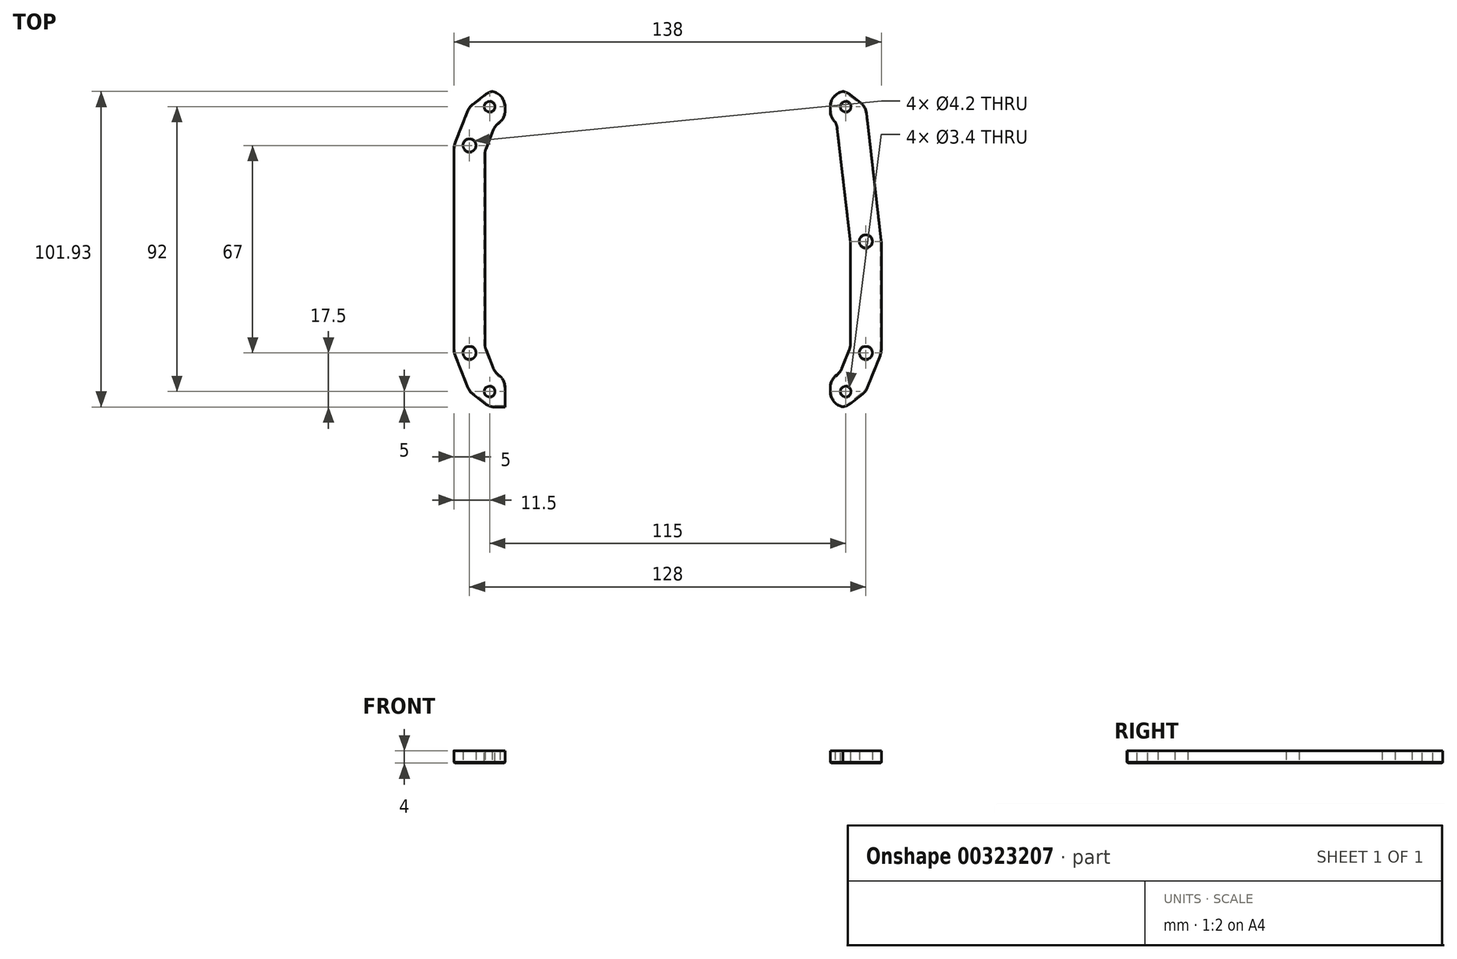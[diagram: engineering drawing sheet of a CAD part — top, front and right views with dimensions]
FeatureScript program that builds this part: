
annotation { "Feature Type Name" : "Feature", "Feature Type Description" : "" }
export const myFeature = defineFeature(function(context is Context, id is Id, definition is map)
    precondition{}
    {
        {
            var Q0;
            Q0=qCreatedBy(makeId("Top.planeOp"),FACE);
            var sketch = newSketch(context, id + "F0", { "sketchPlane" : qUnion([Q0])});
            skLineSegment(sketch, "E0", {"start": v(-64, 33.5) * mm, "end": v(-64, -33.5) * mm, "construction": true});
            skLineSegment(sketch, "E1", {"start": v(-64, -33.5) * mm, "end": v(64, -33.5) * mm, "construction": true});
            skLineSegment(sketch, "E2", {"start": v(64, -33.5) * mm, "end": v(64, 2.5) * mm, "construction": true});
            skLineSegment(sketch, "E3", {"start": v(0, 0) * mm, "end": v(0, -33.5) * mm, "construction": true});
            skCircle(sketch, "E4", {"center": v(-64, 33.5) * mm, "radius": 2.1 * mm});
            skCircle(sketch, "E5", {"center": v(-64, -33.5) * mm, "radius": 2.1 * mm});
            skCircle(sketch, "E6", {"center": v(64, -33.5) * mm, "radius": 2.1 * mm});
            skCircle(sketch, "E7", {"center": v(64, 2.5) * mm, "radius": 2.1 * mm});
            skSolve(sketch);
        }
        {
            var Q0;
            Q0=qCreatedBy(makeId("Top.planeOp"),FACE);
            var sketch = newSketch(context, id + "F1", { "sketchPlane" : qUnion([Q0])});
            skLineSegment(sketch, "E8.bottom", {"start": v(57.5, 46) * mm, "end": v(-57.5, 46) * mm, "construction": true});
            skLineSegment(sketch, "E8.top", {"start": v(57.5, -46) * mm, "end": v(-57.5, -46) * mm, "construction": true});
            skLineSegment(sketch, "E8.left", {"start": v(57.5, 46) * mm, "end": v(57.5, -46) * mm, "construction": true});
            skLineSegment(sketch, "E8.right", {"start": v(-57.5, 46) * mm, "end": v(-57.5, -46) * mm, "construction": true});
            skPoint(sketch, "E8.middle", {"position": v(0, 0) * mm});
            skCircle(sketch, "E9", {"center": v(-57.5, 46) * mm, "radius": 2.1 * mm});
            skCircle(sketch, "E10", {"center": v(57.5, 46) * mm, "radius": 2.1 * mm});
            skCircle(sketch, "E11", {"center": v(57.5, -46) * mm, "radius": 2.1 * mm});
            skCircle(sketch, "E12", {"center": v(-57.5, -46) * mm, "radius": 2.1 * mm});
            skSolve(sketch);
        }
        {
            var Q0;
            Q0=qCreatedBy(makeId("Top.planeOp"),FACE);
            var sketch = newSketch(context, id + "F2", { "sketchPlane" : qUnion([Q0])});
            skLineSegment(sketch, "E13", {"start": v(-69, 33.5) * mm, "end": v(-69, -33.5) * mm});
            skLineSegment(sketch, "E14", {"start": v(-57.5, -51) * mm, "end": v(57.5, -51) * mm});
            skLineSegment(sketch, "E15", {"start": v(69, -33.5) * mm, "end": v(69, 2.5) * mm});
            skLineSegment(sketch, "E16", {"start": v(57.5, 51) * mm, "end": v(-57.5, 51) * mm});
            skLineSegment(sketch, "E17", {"start": v(-69, 33.5) * mm, "end": v(-64, 46) * mm});
            skLineSegment(sketch, "E18", {"start": v(-64, 46) * mm, "end": v(-57.5, 51) * mm});
            skLineSegment(sketch, "E19", {"start": v(57.5, 51) * mm, "end": v(64, 46) * mm});
            skLineSegment(sketch, "E20", {"start": v(64, 46) * mm, "end": v(69, 2.5) * mm});
            skLineSegment(sketch, "E21", {"start": v(57.5, -51) * mm, "end": v(64, -46) * mm});
            skLineSegment(sketch, "E22", {"start": v(64, -46) * mm, "end": v(69, -33.5) * mm});
            skLineSegment(sketch, "E23", {"start": v(-57.5, -51) * mm, "end": v(-64, -46) * mm});
            skLineSegment(sketch, "E24", {"start": v(-64, -46) * mm, "end": v(-69, -33.5) * mm});
            skLineSegment(sketch, "E25.0", {"start": v(55.73, -39.74) * mm, "end": v(59, -31.57) * mm});
            skLineSegment(sketch, "E25.1", {"start": v(-55.73, 39.74) * mm, "end": v(-54.1, 41) * mm});
            skLineSegment(sketch, "E25.2", {"start": v(54.1, 41) * mm, "end": v(-54.1, 41) * mm});
            skLineSegment(sketch, "E25.3", {"start": v(54.1, 41) * mm, "end": v(54.55, 40.65) * mm});
            skLineSegment(sketch, "E25.4", {"start": v(54.55, 40.65) * mm, "end": v(59, 1.93) * mm});
            skLineSegment(sketch, "E25.5", {"start": v(-59, 31.57) * mm, "end": v(-55.73, 39.74) * mm});
            skLineSegment(sketch, "E25.6", {"start": v(59, -31.57) * mm, "end": v(59, 1.93) * mm});
            skLineSegment(sketch, "E25.7", {"start": v(-59, 31.57) * mm, "end": v(-59, -31.57) * mm});
            skLineSegment(sketch, "E25.8", {"start": v(-55.73, -39.74) * mm, "end": v(-59, -31.57) * mm});
            skLineSegment(sketch, "E25.9", {"start": v(-54.1, -41) * mm, "end": v(-55.73, -39.74) * mm});
            skLineSegment(sketch, "E25.10", {"start": v(-54.1, -41) * mm, "end": v(54.1, -41) * mm});
            skLineSegment(sketch, "E25.11", {"start": v(54.1, -41) * mm, "end": v(55.73, -39.74) * mm});
            skSolve(sketch);
        }
        {
            var Q0;
            Q0=makeQuery(id+"F2.imprint","IMPRINT",FACE,{"disambiguationData":[TD([[makeQuery(id+"F2.imprint","IMPRINT",EDGE,{"derivedFrom":sQuery(id+"F2.wireOp",EDGE,"E13")}),1.0]])]});
            extrude(context, id + "F3", {"entities" : qUnion([Q0]), "depth" : 4 * mm});
        }
        {
            var Q0;
            Q0=qSketchRegion(id+"F0",true);
            extrude(context, id + "F4", {"entities" : qUnion([Q0]), "operationType" : NewBodyOperationType.REMOVE, "endBound" : BoundingType.THROUGH_ALL, "depth" : 25 * mm});
        }
        {
            var Q0;
            Q0=makeQuery(id+"F3.opExtrude","CAP_FACE",FACE,{"disambiguationData":[OSD([sQuery(id+"F2.wireOp",EDGE,"E13"),sQuery(id+"F2.wireOp",EDGE,"E14"),sQuery(id+"F2.wireOp",EDGE,"E15"),sQuery(id+"F2.wireOp",EDGE,"E16"),sQuery(id+"F2.wireOp",EDGE,"E17"),sQuery(id+"F2.wireOp",EDGE,"E18"),sQuery(id+"F2.wireOp",EDGE,"E19"),sQuery(id+"F2.wireOp",EDGE,"E20"),sQuery(id+"F2.wireOp",EDGE,"E21"),sQuery(id+"F2.wireOp",EDGE,"E22"),sQuery(id+"F2.wireOp",EDGE,"E23"),sQuery(id+"F2.wireOp",EDGE,"E24"),sQuery(id+"F2.wireOp",EDGE,"E25.0"),sQuery(id+"F2.wireOp",EDGE,"E25.1"),sQuery(id+"F2.wireOp",EDGE,"E25.2"),sQuery(id+"F2.wireOp",EDGE,"E25.3"),sQuery(id+"F2.wireOp",EDGE,"E25.4"),sQuery(id+"F2.wireOp",EDGE,"E25.5"),sQuery(id+"F2.wireOp",EDGE,"E25.6"),sQuery(id+"F2.wireOp",EDGE,"E25.7"),sQuery(id+"F2.wireOp",EDGE,"E25.8"),sQuery(id+"F2.wireOp",EDGE,"E25.9"),sQuery(id+"F2.wireOp",EDGE,"E25.10"),sQuery(id+"F2.wireOp",EDGE,"E25.11")])],"isStart":false});
            var sketch = newSketch(context, id + "F5", { "sketchPlane" : qUnion([Q0])});
            skCircle(sketch, "E26", {"center": v(-57.5, 46) * mm, "radius": 1.7 * mm});
            skCircle(sketch, "E27", {"center": v(57.5, 46) * mm, "radius": 1.7 * mm});
            skCircle(sketch, "E28", {"center": v(57.5, -46) * mm, "radius": 1.7 * mm});
            skCircle(sketch, "E29", {"center": v(-57.5, -46) * mm, "radius": 1.7 * mm});
            skSolve(sketch);
        }
        {
            var Q0;
            Q0=qSketchRegion(id+"F5",true);
            extrude(context, id + "F6", {"entities" : qUnion([Q0]), "operationType" : NewBodyOperationType.REMOVE, "endBound" : BoundingType.THROUGH_ALL, "oppositeDirection" : true, "depth" : 25 * mm});
        }
        {
            var Q0;
            Q0=makeQuery(id+"F3.opExtrude","SWEPT_FACE",FACE,{"disambiguationData":[OSD([sQuery(id+"F2.wireOp",EDGE,"E14")])]});
            var sketch = newSketch(context, id + "F7", { "sketchPlane" : qUnion([Q0])});
            skLineSegment(sketch, "E30.bottom", {"start": v(-52.5, 0) * mm, "end": v(52.5, 0) * mm});
            skLineSegment(sketch, "E30.top", {"start": v(-52.5, 4) * mm, "end": v(52.5, 4) * mm});
            skLineSegment(sketch, "E30.left", {"start": v(-52.5, 0) * mm, "end": v(-52.5, 4) * mm});
            skLineSegment(sketch, "E30.right", {"start": v(52.5, 0) * mm, "end": v(52.5, 4) * mm});
            skSolve(sketch);
        }
        {
            var Q0;
            Q0=qSketchRegion(id+"F7",true);
            extrude(context, id + "F8", {"entities" : qUnion([Q0]), "operationType" : NewBodyOperationType.REMOVE, "endBound" : BoundingType.THROUGH_ALL, "oppositeDirection" : true, "depth" : 25 * mm});
        }
        {
            var Q0;
            Q0=makeQuery(id+"F8.boolean.opBoolean","COPY",EDGE,{"derivedFrom":makeQuery(id+"F8.opExtrude","CAP_EDGE",EDGE,{"disambiguationData":[OSD([sQuery(id+"F7.wireOp",EDGE,"E30.left")])],"isStart":true})});
            var Q1;
            Q1=makeQuery(id+"F3.opExtrude","SWEPT_EDGE",EDGE,{"disambiguationData":[OSD([sQuery(id+"F2.wireOp",EDGE,"E14"),sQuery(id+"F2.wireOp",EDGE,"E23")])]});
            var Q2;
            Q2=makeQuery(id+"F3.opExtrude","SWEPT_EDGE",EDGE,{"disambiguationData":[OSD([sQuery(id+"F2.wireOp",EDGE,"E23"),sQuery(id+"F2.wireOp",EDGE,"E24")])]});
            var Q3;
            Q3=makeQuery(id+"F3.opExtrude","SWEPT_EDGE",EDGE,{"disambiguationData":[OSD([sQuery(id+"F2.wireOp",EDGE,"E13"),sQuery(id+"F2.wireOp",EDGE,"E24")])]});
            var Q4;
            Q4=makeQuery(id+"F8.boolean.opBoolean","INTERSECT",EDGE,{"derivedFrom":[makeQuery(id+"F3.opExtrude","SWEPT_FACE",FACE,{"disambiguationData":[OSD([sQuery(id+"F2.wireOp",EDGE,"E25.10")])]}),makeQuery(id+"F8.opExtrude","SWEPT_FACE",FACE,{"disambiguationData":[OSD([sQuery(id+"F7.wireOp",EDGE,"E30.left")])]})]});
            var Q5;
            Q5=makeQuery(id+"F3.opExtrude","SWEPT_EDGE",EDGE,{"disambiguationData":[OSD([sQuery(id+"F2.wireOp",EDGE,"E25.8"),sQuery(id+"F2.wireOp",EDGE,"E25.9")])]});
            var Q6;
            Q6=makeQuery(id+"F3.opExtrude","SWEPT_EDGE",EDGE,{"disambiguationData":[OSD([sQuery(id+"F2.wireOp",EDGE,"E25.7"),sQuery(id+"F2.wireOp",EDGE,"E25.8")])]});
            var Q7;
            Q7=makeQuery(id+"F3.opExtrude","SWEPT_EDGE",EDGE,{"disambiguationData":[OSD([sQuery(id+"F2.wireOp",EDGE,"E25.5"),sQuery(id+"F2.wireOp",EDGE,"E25.7")])]});
            var Q8;
            Q8=makeQuery(id+"F8.boolean.opBoolean","INTERSECT",EDGE,{"derivedFrom":[makeQuery(id+"F3.opExtrude","SWEPT_FACE",FACE,{"disambiguationData":[OSD([sQuery(id+"F2.wireOp",EDGE,"E25.2")])]}),makeQuery(id+"F8.opExtrude","SWEPT_FACE",FACE,{"disambiguationData":[OSD([sQuery(id+"F7.wireOp",EDGE,"E30.left")])]})]});
            var Q9;
            Q9=makeQuery(id+"F3.opExtrude","SWEPT_EDGE",EDGE,{"disambiguationData":[OSD([sQuery(id+"F2.wireOp",EDGE,"E25.1"),sQuery(id+"F2.wireOp",EDGE,"E25.5")])]});
            var Q10;
            Q10=makeQuery(id+"F8.boolean.opBoolean","INTERSECT",EDGE,{"derivedFrom":[makeQuery(id+"F3.opExtrude","SWEPT_FACE",FACE,{"disambiguationData":[OSD([sQuery(id+"F2.wireOp",EDGE,"E16")])]}),makeQuery(id+"F8.opExtrude","SWEPT_FACE",FACE,{"disambiguationData":[OSD([sQuery(id+"F7.wireOp",EDGE,"E30.left")])]})]});
            var Q11;
            Q11=makeQuery(id+"F3.opExtrude","SWEPT_EDGE",EDGE,{"disambiguationData":[OSD([sQuery(id+"F2.wireOp",EDGE,"E16"),sQuery(id+"F2.wireOp",EDGE,"E18")])]});
            var Q12;
            Q12=makeQuery(id+"F3.opExtrude","SWEPT_EDGE",EDGE,{"disambiguationData":[OSD([sQuery(id+"F2.wireOp",EDGE,"E17"),sQuery(id+"F2.wireOp",EDGE,"E18")])]});
            var Q13;
            Q13=makeQuery(id+"F3.opExtrude","SWEPT_EDGE",EDGE,{"disambiguationData":[OSD([sQuery(id+"F2.wireOp",EDGE,"E13"),sQuery(id+"F2.wireOp",EDGE,"E17")])]});
            var Q14;
            Q14=makeQuery(id+"F3.opExtrude","SWEPT_EDGE",EDGE,{"disambiguationData":[OSD([sQuery(id+"F2.wireOp",EDGE,"E14"),sQuery(id+"F2.wireOp",EDGE,"E21")])]});
            var Q15;
            Q15=makeQuery(id+"F3.opExtrude","SWEPT_EDGE",EDGE,{"disambiguationData":[OSD([sQuery(id+"F2.wireOp",EDGE,"E21"),sQuery(id+"F2.wireOp",EDGE,"E22")])]});
            var Q16;
            Q16=makeQuery(id+"F3.opExtrude","SWEPT_EDGE",EDGE,{"disambiguationData":[OSD([sQuery(id+"F2.wireOp",EDGE,"E15"),sQuery(id+"F2.wireOp",EDGE,"E22")])]});
            var Q17;
            Q17=makeQuery(id+"F8.boolean.opBoolean","COPY",EDGE,{"derivedFrom":makeQuery(id+"F8.opExtrude","CAP_EDGE",EDGE,{"disambiguationData":[OSD([sQuery(id+"F7.wireOp",EDGE,"E30.right")])],"isStart":true})});
            var Q18;
            Q18=makeQuery(id+"F8.boolean.opBoolean","INTERSECT",EDGE,{"derivedFrom":[makeQuery(id+"F3.opExtrude","SWEPT_FACE",FACE,{"disambiguationData":[OSD([sQuery(id+"F2.wireOp",EDGE,"E25.10")])]}),makeQuery(id+"F8.opExtrude","SWEPT_FACE",FACE,{"disambiguationData":[OSD([sQuery(id+"F7.wireOp",EDGE,"E30.right")])]})]});
            var Q19;
            Q19=makeQuery(id+"F3.opExtrude","SWEPT_EDGE",EDGE,{"disambiguationData":[OSD([sQuery(id+"F2.wireOp",EDGE,"E25.0"),sQuery(id+"F2.wireOp",EDGE,"E25.11")])]});
            var Q20;
            Q20=makeQuery(id+"F3.opExtrude","SWEPT_EDGE",EDGE,{"disambiguationData":[OSD([sQuery(id+"F2.wireOp",EDGE,"E25.0"),sQuery(id+"F2.wireOp",EDGE,"E25.6")])]});
            var Q21;
            Q21=makeQuery(id+"F3.opExtrude","SWEPT_EDGE",EDGE,{"disambiguationData":[OSD([sQuery(id+"F2.wireOp",EDGE,"E25.4"),sQuery(id+"F2.wireOp",EDGE,"E25.6")])]});
            var Q22;
            Q22=makeQuery(id+"F3.opExtrude","SWEPT_EDGE",EDGE,{"disambiguationData":[OSD([sQuery(id+"F2.wireOp",EDGE,"E25.3"),sQuery(id+"F2.wireOp",EDGE,"E25.4")])]});
            var Q23;
            Q23=makeQuery(id+"F8.boolean.opBoolean","INTERSECT",EDGE,{"derivedFrom":[makeQuery(id+"F3.opExtrude","SWEPT_FACE",FACE,{"disambiguationData":[OSD([sQuery(id+"F2.wireOp",EDGE,"E25.2")])]}),makeQuery(id+"F8.opExtrude","SWEPT_FACE",FACE,{"disambiguationData":[OSD([sQuery(id+"F7.wireOp",EDGE,"E30.right")])]})]});
            var Q24;
            Q24=makeQuery(id+"F8.boolean.opBoolean","INTERSECT",EDGE,{"derivedFrom":[makeQuery(id+"F3.opExtrude","SWEPT_FACE",FACE,{"disambiguationData":[OSD([sQuery(id+"F2.wireOp",EDGE,"E16")])]}),makeQuery(id+"F8.opExtrude","SWEPT_FACE",FACE,{"disambiguationData":[OSD([sQuery(id+"F7.wireOp",EDGE,"E30.right")])]})]});
            var Q25;
            Q25=makeQuery(id+"F3.opExtrude","SWEPT_EDGE",EDGE,{"disambiguationData":[OSD([sQuery(id+"F2.wireOp",EDGE,"E16"),sQuery(id+"F2.wireOp",EDGE,"E19")])]});
            var Q26;
            Q26=makeQuery(id+"F3.opExtrude","SWEPT_EDGE",EDGE,{"disambiguationData":[OSD([sQuery(id+"F2.wireOp",EDGE,"E19"),sQuery(id+"F2.wireOp",EDGE,"E20")])]});
            var Q27;
            Q27=makeQuery(id+"F3.opExtrude","SWEPT_EDGE",EDGE,{"disambiguationData":[OSD([sQuery(id+"F2.wireOp",EDGE,"E15"),sQuery(id+"F2.wireOp",EDGE,"E20")])]});
            fillet(context, id + "F9", {"entities" : qUnion([Q0, Q1, Q2, Q3, Q4, Q5, Q6, Q7, Q8, Q9, Q10, Q11, Q12, Q13, Q14, Q15, Q16, Q17, Q18, Q19, Q20, Q21, Q22, Q23, Q24, Q25, Q26, Q27]), "radius" : 5 * mm, "tangentPropagation" : true, "allowEdgeOverflow" : false});
        }
        {
            var Q0;
            {var subQ0=sQuery(id+"F2.wireOp",EDGE,"E25.2");var subQ1=sQuery(id+"F2.wireOp",EDGE,"E24");var subQ2=sQuery(id+"F2.wireOp",EDGE,"E18");var subQ3=sQuery(id+"F2.wireOp",EDGE,"E13");var subQ4=sQuery(id+"F2.wireOp",EDGE,"E23");var subQ5=sQuery(id+"F2.wireOp",EDGE,"E14");var subQ6=sQuery(id+"F2.wireOp",EDGE,"E25.5");var subQ7=sQuery(id+"F2.wireOp",EDGE,"E16");var subQ8=sQuery(id+"F2.wireOp",EDGE,"E25.9");var subQ9=sQuery(id+"F2.wireOp",EDGE,"E25.1");var subQ10=sQuery(id+"F2.wireOp",EDGE,"E17");var subQ11=sQuery(id+"F2.wireOp",EDGE,"E25.10");var subQ12=sQuery(id+"F2.wireOp",EDGE,"E25.7");var subQ13=sQuery(id+"F2.wireOp",EDGE,"E25.8");Q0=makeQuery(id+"F8.boolean.opBoolean","SPLIT",FACE,{"disambiguationData":[TD([makeQuery(id+"F3.opExtrude","SWEPT_FACE",FACE,{"disambiguationData":[OSD([subQ3])]})])],"derivedFrom":makeQuery(id+"F3.opExtrude","CAP_FACE",FACE,{"disambiguationData":[OSD([subQ3,subQ5,sQuery(id+"F2.wireOp",EDGE,"E15"),subQ7,subQ10,subQ2,sQuery(id+"F2.wireOp",EDGE,"E19"),sQuery(id+"F2.wireOp",EDGE,"E20"),sQuery(id+"F2.wireOp",EDGE,"E21"),sQuery(id+"F2.wireOp",EDGE,"E22"),subQ4,subQ1,sQuery(id+"F2.wireOp",EDGE,"E25.0"),subQ9,subQ0,sQuery(id+"F2.wireOp",EDGE,"E25.3"),sQuery(id+"F2.wireOp",EDGE,"E25.4"),subQ6,sQuery(id+"F2.wireOp",EDGE,"E25.6"),subQ12,subQ13,subQ8,subQ11,sQuery(id+"F2.wireOp",EDGE,"E25.11")])],"isStart":true})});}
            var Q1;
            {var subQ0=sQuery(id+"F2.wireOp",EDGE,"E25.2");var subQ1=sQuery(id+"F2.wireOp",EDGE,"E22");var subQ2=sQuery(id+"F2.wireOp",EDGE,"E21");var subQ3=sQuery(id+"F2.wireOp",EDGE,"E20");var subQ4=sQuery(id+"F2.wireOp",EDGE,"E25.3");var subQ5=sQuery(id+"F2.wireOp",EDGE,"E14");var subQ6=sQuery(id+"F2.wireOp",EDGE,"E15");var subQ7=sQuery(id+"F2.wireOp",EDGE,"E25.0");var subQ8=sQuery(id+"F2.wireOp",EDGE,"E16");var subQ9=sQuery(id+"F2.wireOp",EDGE,"E19");var subQ10=sQuery(id+"F2.wireOp",EDGE,"E25.4");var subQ11=sQuery(id+"F2.wireOp",EDGE,"E25.6");var subQ12=sQuery(id+"F2.wireOp",EDGE,"E25.10");var subQ13=sQuery(id+"F2.wireOp",EDGE,"E25.11");Q1=makeQuery(id+"F8.boolean.opBoolean","SPLIT",FACE,{"disambiguationData":[TD([makeQuery(id+"F3.opExtrude","SWEPT_FACE",FACE,{"disambiguationData":[OSD([subQ6])]})])],"derivedFrom":makeQuery(id+"F3.opExtrude","CAP_FACE",FACE,{"disambiguationData":[OSD([sQuery(id+"F2.wireOp",EDGE,"E13"),subQ5,subQ6,subQ8,sQuery(id+"F2.wireOp",EDGE,"E17"),sQuery(id+"F2.wireOp",EDGE,"E18"),subQ9,subQ3,subQ2,subQ1,sQuery(id+"F2.wireOp",EDGE,"E23"),sQuery(id+"F2.wireOp",EDGE,"E24"),subQ7,sQuery(id+"F2.wireOp",EDGE,"E25.1"),subQ0,subQ4,subQ10,sQuery(id+"F2.wireOp",EDGE,"E25.5"),subQ11,sQuery(id+"F2.wireOp",EDGE,"E25.7"),sQuery(id+"F2.wireOp",EDGE,"E25.8"),sQuery(id+"F2.wireOp",EDGE,"E25.9"),subQ12,subQ13])],"isStart":true})});}
            chamfer(context, id + "F10", {"entities" : qUnion([Q0, Q1]), "width" : 0.3 * mm, "tangentPropagation" : true});
        }
    });
